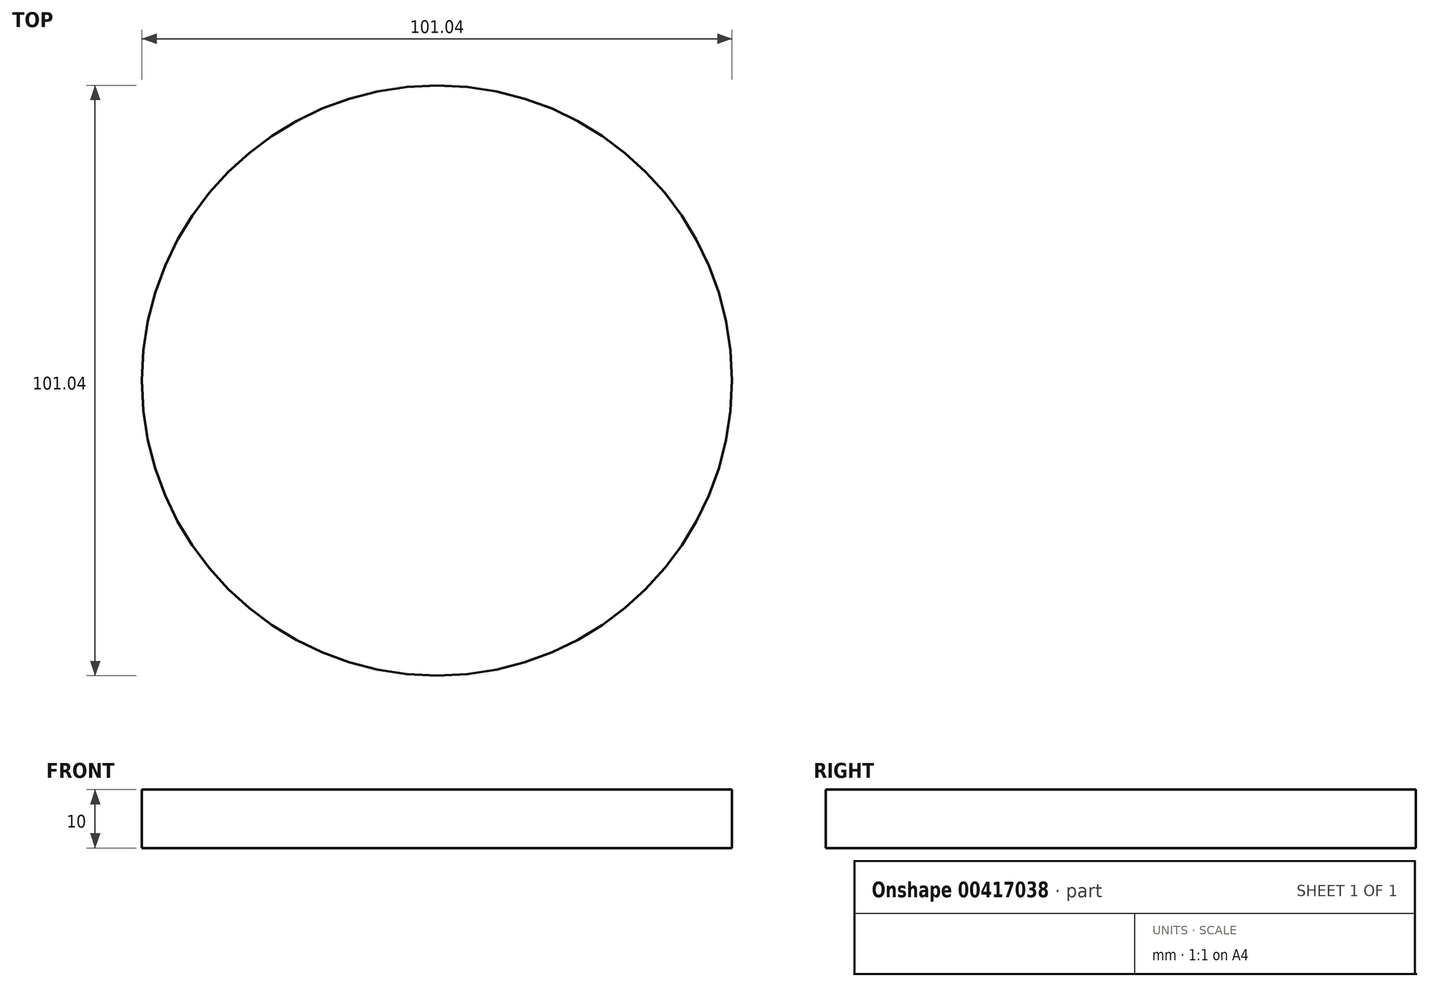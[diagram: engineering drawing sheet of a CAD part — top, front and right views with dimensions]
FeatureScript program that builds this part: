
annotation { "Feature Type Name" : "Feature", "Feature Type Description" : "" }
export const myFeature = defineFeature(function(context is Context, id is Id, definition is map)
    precondition{}
    {
        {
            var Q0;
            Q0=qCreatedBy(makeId("Top.planeOp"),FACE);
            var sketch = newSketch(context, id + "F0", { "sketchPlane" : qUnion([Q0])});
            skCircle(sketch, "E0", {"center": v(0, 0) * mm, "radius": 50.52 * mm});
            skSolve(sketch);
        }
        {
            var Q0;
            Q0=makeQuery(id+"F0.imprint","IMPRINT",FACE,{"disambiguationData":[TD([[makeQuery(id+"F0.imprint","IMPRINT",EDGE,{"derivedFrom":sQuery(id+"F0.wireOp",EDGE,"E0")}),1.0]])]});
            extrude(context, id + "F1", {"entities" : qUnion([Q0]), "depth" : 10 * mm});
        }
    });
